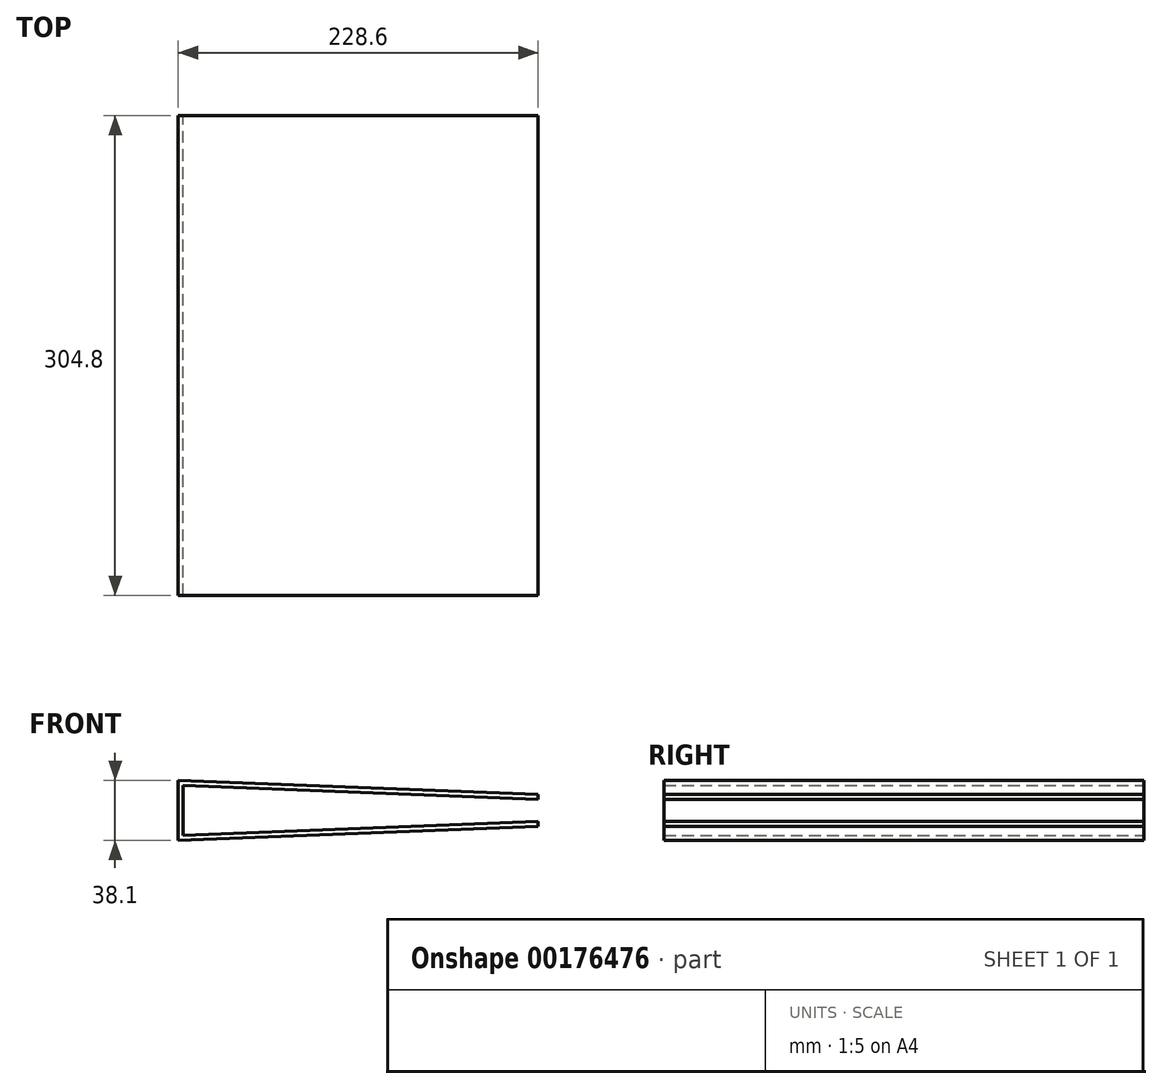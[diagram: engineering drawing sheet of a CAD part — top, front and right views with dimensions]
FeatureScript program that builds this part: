
annotation { "Feature Type Name" : "Feature", "Feature Type Description" : "" }
export const myFeature = defineFeature(function(context is Context, id is Id, definition is map)
    precondition{}
    {
        {
            var Q0;
            Q0=qCreatedBy(makeId("Front.planeOp"),FACE);
            var sketch = newSketch(context, id + "F0", { "sketchPlane" : qUnion([Q0])});
            skLineSegment(sketch, "E0.bottom", {"start": v(-114.3, 19.05) * mm, "end": v(114.3, 19.05) * mm, "construction": true});
            skLineSegment(sketch, "E0.top", {"start": v(-114.3, -19.05) * mm, "end": v(114.3, -19.05) * mm, "construction": true});
            skLineSegment(sketch, "E0.left", {"start": v(-114.3, 19.05) * mm, "end": v(-114.3, -19.05) * mm, "construction": true});
            skPoint(sketch, "E0.middle", {"position": v(0, 0) * mm});
            skLineSegment(sketch, "E1", {"start": v(114.3, -19.05) * mm, "end": v(114.3, 0) * mm, "construction": true});
            skLineSegment(sketch, "E2", {"start": v(114.3, 0) * mm, "end": v(114.3, 19.05) * mm, "construction": true});
            skLineSegment(sketch, "E3", {"start": v(-114.3, -19.05) * mm, "end": v(-114.3, 19.05) * mm});
            skLineSegment(sketch, "E4", {"start": v(114.3, 10.16) * mm, "end": v(-114.3, 19.05) * mm});
            skLineSegment(sketch, "E5", {"start": v(114.3, -10.16) * mm, "end": v(-114.3, -19.05) * mm});
            skLineSegment(sketch, "E6", {"start": v(114.3, 10.16) * mm, "end": v(114.3, 6.99) * mm});
            skLineSegment(sketch, "E7", {"start": v(114.3, -10.16) * mm, "end": v(114.3, -6.99) * mm});
            skLineSegment(sketch, "E8", {"start": v(114.3, 6.98) * mm, "end": v(-111.13, 15.75) * mm});
            skLineSegment(sketch, "E9", {"start": v(114.3, -6.99) * mm, "end": v(-111.13, -15.75) * mm});
            skLineSegment(sketch, "E10", {"start": v(-111.13, 15.75) * mm, "end": v(-111.13, -15.75) * mm});
            skSolve(sketch);
        }
        {
            var Q0;
            Q0 = qSketchRegion(id + "F0", true);
            extrude(context, id + "F1", {"entities" : qUnion([Q0]), "depth" : 304.8 * mm});
        }
    });
